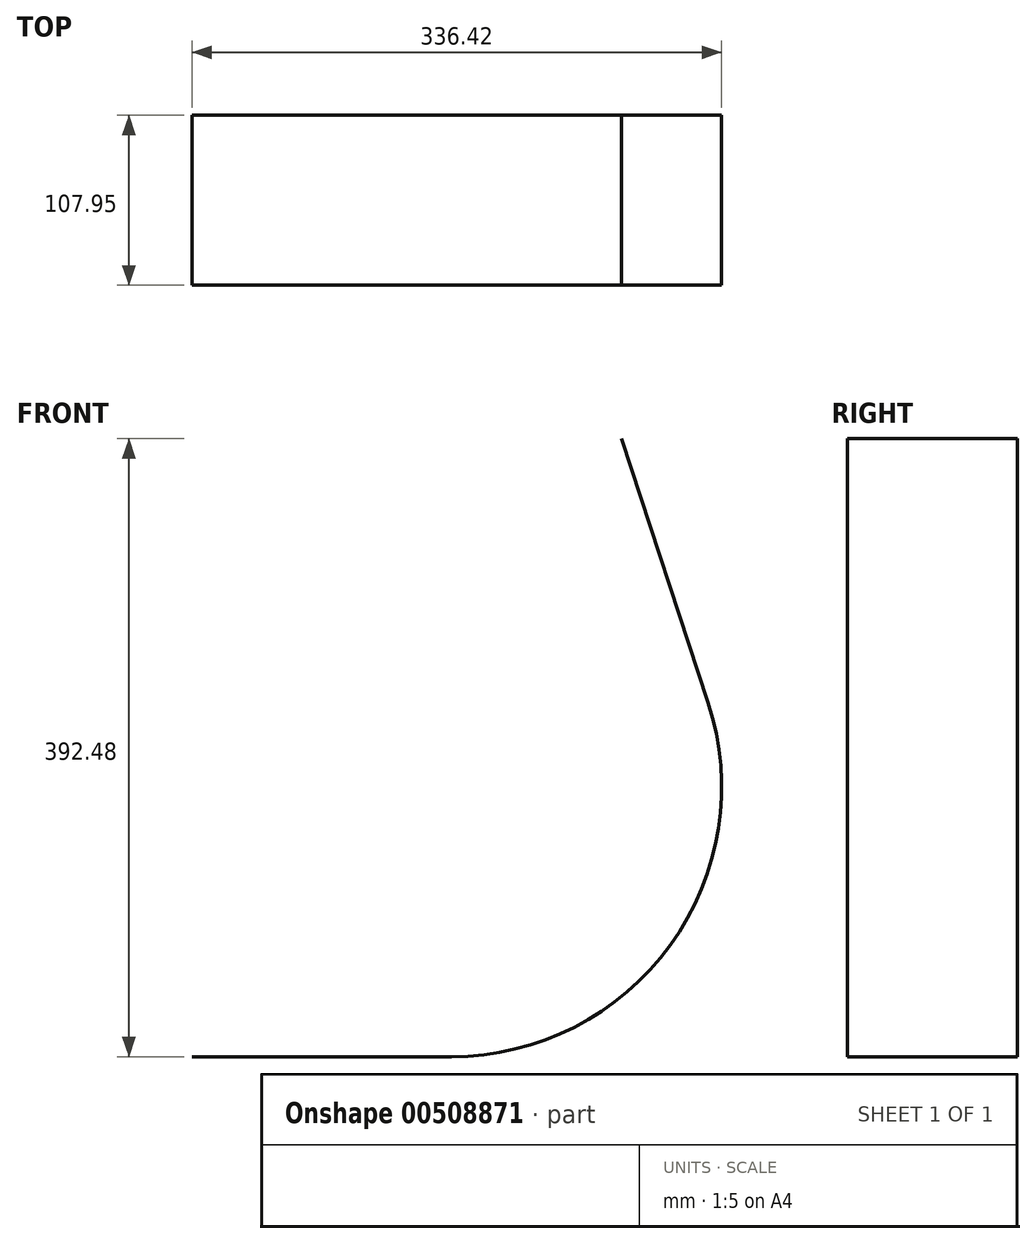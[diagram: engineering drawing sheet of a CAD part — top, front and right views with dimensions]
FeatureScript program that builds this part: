
annotation { "Feature Type Name" : "Feature", "Feature Type Description" : "" }
export const myFeature = defineFeature(function(context is Context, id is Id, definition is map)
    precondition{}
    {
        {
            var Q0;
            Q0=qCreatedBy(makeId("Front.planeOp"),FACE);
            var sketch = newSketch(context, id + "F0", { "sketchPlane" : qUnion([Q0])});
            skCircle(sketch, "E0", {"center": v(-0.1, -1) * mm, "radius": 6.35 * mm});
            skArc(sketch, "E1", {"start": v(162.79, 52.5) * mm, "mid": v(138.77, -101.56) * mm, "end": v(-0.1, -172.45) * mm});
            skCircle(sketch, "E2", {"center": v(-0.1, -1) * mm, "radius": 50.8 * mm, "construction": true});
            skLineSegment(sketch, "E3", {"start": v(162.79, 52.5) * mm, "end": v(107.75, 220.03) * mm});
            skLineSegment(sketch, "E4", {"start": v(-0.1, -172.45) * mm, "end": v(-165.07, -172.45) * mm});
            skSolve(sketch);
        }
        {
            var Q0;
            Q0=qSketchRegion(id+"F0",true);
            var Q1;
            Q1=sQuery(id+"F0.wireOp",EDGE,"E4");
            var Q2;
            Q2=sQuery(id+"F0.wireOp",EDGE,"E1");
            var Q3;
            Q3=sQuery(id+"F0.wireOp",EDGE,"E3");
            extrude(context, id + "F1", {"entities" : qUnion([Q0]), "bodyType" : ToolBodyType.SURFACE, "surfaceEntities" : qUnion([Q1, Q2, Q3]), "depth" : 107.95 * mm});
        }
    });
